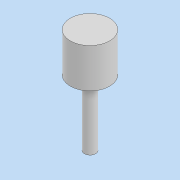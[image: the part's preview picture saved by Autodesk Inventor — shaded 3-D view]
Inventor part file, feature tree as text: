
AUTODESK INVENTOR PART (.ipt)
format: ipt  version: 2022 (Build 260153070, 153G)  size: 102,400 bytes
history: native  units: mm
features: revolve x1, sketch x1
ambient origin geometry x8: Origin, YZ Plane, XZ Plane, XY Plane, X Axis, Y Axis, Z Axis, Center Point
bodies: Solid1 (feature_tree)
feature tree (2):
  revolve  "Revolution1"  [1 undecoded]
  sketch  "Sketch1"  dims[d0=1.45mm d1=15.0mm d2=11.34464mm d4=10.0mm d5=90.0deg d6=5.0mm]
note: 1 required parameter value undecoded (feature->parameter linkage not recoverable at this tier; creation-order binding heuristic only, values carry confidence <= 0.55)
